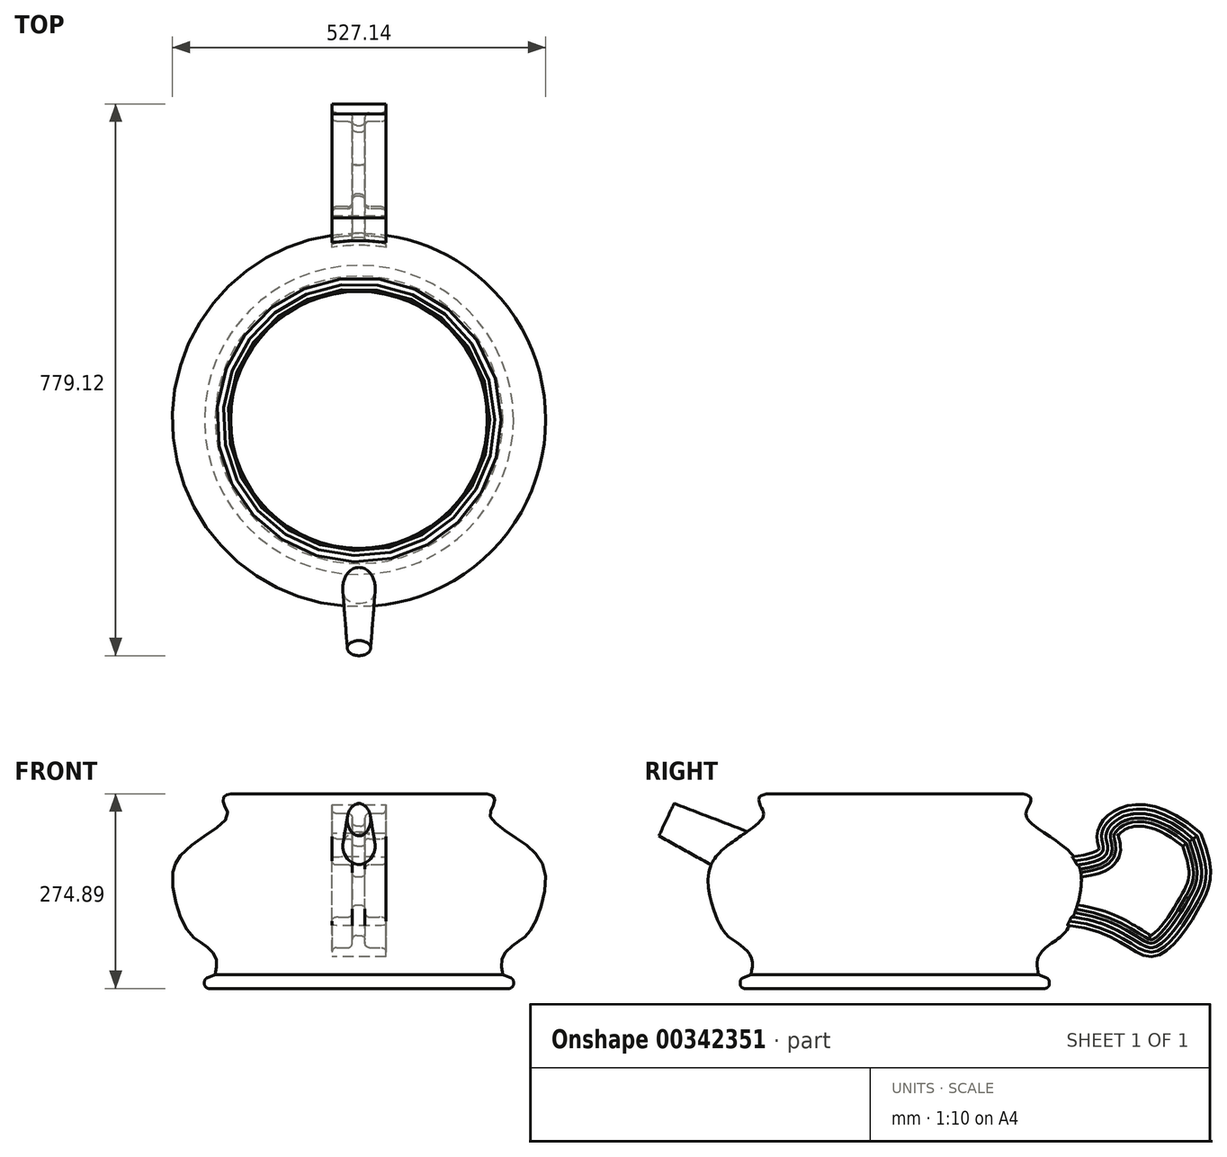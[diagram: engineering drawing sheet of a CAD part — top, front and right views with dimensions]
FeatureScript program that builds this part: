
annotation { "Feature Type Name" : "Feature", "Feature Type Description" : "" }
export const myFeature = defineFeature(function(context is Context, id is Id, definition is map)
    precondition{}
    {
        {
            var Q0;
            Q0=qCreatedBy(makeId("Front.planeOp"),FACE);
            var sketch = newSketch(context, id + "F0", { "sketchPlane" : qUnion([Q0])});
            skLineSegment(sketch, "E0.bottom", {"start": v(-31.75, 4.66) * mm, "end": v(-15.87, 4.66) * mm});
            skLineSegment(sketch, "E0.top", {"start": v(-38.1, -8.04) * mm, "end": v(38.1, -8.04) * mm});
            skLineSegment(sketch, "E0.left", {"start": v(-38.1, -1.7) * mm, "end": v(-38.1, -8.04) * mm});
            skLineSegment(sketch, "E0.right", {"start": v(38.1, -1.7) * mm, "end": v(38.1, -8.04) * mm});
            skPoint(sketch, "E0.middle", {"position": v(0, -1.7) * mm});
            skLineSegment(sketch, "E1", {"start": v(-9.52, 11) * mm, "end": v(-9.52, 16.17) * mm});
            skLineSegment(sketch, "E2", {"start": v(-3.17, 22.52) * mm, "end": v(2.14, 22.52) * mm});
            skLineSegment(sketch, "E3", {"start": v(8.5, 16.17) * mm, "end": v(8.5, 11) * mm});
            skLineSegment(sketch, "E4.trimOffspring", {"start": v(14.84, 4.66) * mm, "end": v(31.75, 4.66) * mm});
            skPoint(sketch, "E5.visualSharp", {"position": v(-9.52, 4.66) * mm});
            skArc(sketch, "E5.filletArc", {"start": v(-15.87, 4.66) * mm, "mid": v(-11.38, 6.52) * mm, "end": v(-9.52, 11) * mm});
            skPoint(sketch, "E6.visualSharp", {"position": v(-38.1, 4.66) * mm});
            skArc(sketch, "E6.filletArc", {"start": v(-31.75, 4.66) * mm, "mid": v(-36.24, 2.8) * mm, "end": v(-38.1, -1.7) * mm});
            skPoint(sketch, "E7.visualSharp", {"position": v(-9.52, 22.52) * mm});
            skArc(sketch, "E7.filletArc", {"start": v(-3.17, 22.52) * mm, "mid": v(-7.66, 20.66) * mm, "end": v(-9.52, 16.17) * mm});
            skPoint(sketch, "E8.visualSharp", {"position": v(8.5, 22.52) * mm});
            skArc(sketch, "E8.filletArc", {"start": v(8.5, 16.17) * mm, "mid": v(6.63, 20.66) * mm, "end": v(2.14, 22.52) * mm});
            skPoint(sketch, "E9.visualSharp", {"position": v(8.5, 4.66) * mm});
            skArc(sketch, "E9.filletArc", {"start": v(8.5, 11) * mm, "mid": v(10.35, 6.52) * mm, "end": v(14.84, 4.66) * mm});
            skPoint(sketch, "E10.visualSharp", {"position": v(38.1, 4.66) * mm});
            skArc(sketch, "E10.filletArc", {"start": v(38.1, -1.7) * mm, "mid": v(36.24, 2.8) * mm, "end": v(31.75, 4.66) * mm});
            skSolve(sketch);
        }
        {
            var Q0;
            Q0=qCreatedBy(makeId("Right.planeOp"),FACE);
            var sketch = newSketch(context, id + "F1", { "sketchPlane" : qUnion([Q0])});
            skFitSpline(sketch, "E11", {"points": [v(0, 0) * mm, v(124.08, -43.75) * mm, v(181.99, 24.07) * mm, v(182.75, 117.02) * mm], "startDerivative": vector(639.17, -56.46) * mm, "endDerivative": vector(-187.27, 486.91) * mm});
            skFitSpline(sketch, "E12", {"points": [v(182.75, 117.02) * mm, v(50.93, 119.3) * mm, v(0, 79.75) * mm], "startDerivative": vector(-384.56, 341.83) * mm, "endDerivative": vector(-537.9, -60.6) * mm});
            skSolve(sketch);
        }
        {
            var Q0;
            Q0=makeQuery(id+"F0.imprint","IMPRINT",FACE,{"disambiguationData":[TD([[makeQuery(id+"F0.imprint","IMPRINT",EDGE,{"derivedFrom":sQuery(id+"F0.wireOp",EDGE,"E0.bottom")}),-1.0]])]});
            var Q1;
            Q1=sQuery(id+"F1.wireOp",EDGE,"E11");
            var Q2;
            Q2=sQuery(id+"F1.wireOp",EDGE,"E12");
            sweep(context, id + "F2", {"profiles" : qUnion([Q0]), "path" : qUnion([Q1, Q2])});
        }
        {
            var Q0;
            Q0=qCreatedBy(makeId("Right.planeOp"),FACE);
            var sketch = newSketch(context, id + "F3", { "sketchPlane" : qUnion([Q0])});
            skFitSpline(sketch, "E13", {"points": [v(-39.6, -77.81) * mm, v(-39.95, -52.85) * mm, v(-18.46, -31.35) * mm, v(0, -14.7) * mm, v(20.03, 66.77) * mm, v(-19.15, 114.27) * mm, v(-57.29, 146.17) * mm, v(-53.13, 160.73) * mm, v(-51.4, 172.52) * mm, v(-61.45, 177.72) * mm], "startDerivative": vector(-55.52, 258.94) * mm, "endDerivative": vector(-190.64, 53.58) * mm});
            skLineSegment(sketch, "E14", {"start": v(-61.45, 177.72) * mm, "end": v(-242.7, 177.72) * mm});
            skLineSegment(sketch, "E15", {"start": v(-242.7, 177.72) * mm, "end": v(-242.7, -77.81) * mm});
            skLineSegment(sketch, "E16", {"start": v(-242.7, -77.81) * mm, "end": v(-242.7, -97.17) * mm});
            skLineSegment(sketch, "E17", {"start": v(-242.7, -97.17) * mm, "end": v(-30.83, -97.17) * mm});
            skLineSegment(sketch, "E18", {"start": v(-24.48, -90.82) * mm, "end": v(-24.48, -87.96) * mm});
            skLineSegment(sketch, "E19", {"start": v(-28.56, -82.02) * mm, "end": v(-39.6, -77.81) * mm});
            skPoint(sketch, "E20.visualSharp", {"position": v(-24.48, -83.58) * mm});
            skArc(sketch, "E20.filletArc", {"start": v(-24.48, -87.96) * mm, "mid": v(-25.6, -84.35) * mm, "end": v(-28.56, -82.02) * mm});
            skPoint(sketch, "E21.visualSharp", {"position": v(-24.48, -97.17) * mm});
            skArc(sketch, "E21.filletArc", {"start": v(-30.83, -97.17) * mm, "mid": v(-26.34, -95.31) * mm, "end": v(-24.48, -90.82) * mm});
            skLineSegment(sketch, "E22", {"start": v(-242.7, 17.38) * mm, "end": v(-242.7, -185.75) * mm, "construction": true});
            skSolve(sketch);
        }
        {
            var Q0;
            Q0=makeQuery(id+"F3.imprint","IMPRINT",FACE,{"disambiguationData":[TD([[makeQuery(id+"F3.imprint","IMPRINT",EDGE,{"derivedFrom":sQuery(id+"F3.wireOp",EDGE,"E13")}),1.0]])]});
            var Q1;
            Q1=sQuery(id+"F3.wireOp",EDGE,"E22");
            revolve(context, id + "F4", {"operationType" : NewBodyOperationType.ADD, "entities" : qUnion([Q0]), "axis" : qUnion([Q1]), "revolveType" : RevolveType.FULL});
        }
        {
            var Q0;
            Q0=qCreatedBy(makeId("Front.planeOp"),FACE);
            cPlane(context, id + "F5", {"entities" : qUnion([Q0]), "cplaneType" : CPlaneType.OFFSET, "offset" : 490.73 * mm, "width" : 152.4 * mm, "height" : 152.4 * mm});
        }
        {
            var Q0;
            Q0=qCreatedBy(id+"F5.planeOp",FACE);
            var sketch = newSketch(context, id + "F6", { "sketchPlane" : qUnion([Q0])});
            skEllipse(sketch, "E23", {"center": v(0, 103.75) * mm, "majorRadius": 60.74 * mm, "minorRadius": 35.53 * mm, "majorAxis": v(0, -1)});
            skSolve(sketch);
        }
        {
            var Q0;
            Q0=qCreatedBy(id+"F5.planeOp",FACE);
            var sketch = newSketch(context, id + "F7", { "sketchPlane" : qUnion([Q0])});
            skLineSegment(sketch, "E24", {"start": v(-73.56, 0) * mm, "end": v(75.93, 0) * mm, "construction": true});
            skSolve(sketch);
        }
        {
            var Q0;
            Q0 = qBodyType(qCreatedBy(id + "F7" ,EDGE), BodyType.WIRE);
            cPlane(context, id + "F8", {"entities" : qUnion([Q0]), "cplaneType" : CPlaneType.LINE_ANGLE, "offset" : 25.4 * mm, "angle" : 25 * degree, "oppositeDirection" : true, "width" : 152.4 * mm, "height" : 152.4 * mm});
        }
        {
            var Q0;
            Q0=qCreatedBy(id+"F8.planeOp",FACE);
            var sketch = newSketch(context, id + "F9", { "sketchPlane" : qUnion([Q0])});
            skEllipse(sketch, "E25", {"center": v(0, -110.82) * mm, "majorRadius": 34.14 * mm, "minorRadius": 25.4 * mm, "majorAxis": v(0, 1)});
            skSolve(sketch);
        }
        {
            var Q0;
            Q0 = qSketchRegion(id + "F9", true);
            extrude(context, id + "F10", {"entities" : qUnion([Q0]), "operationType" : NewBodyOperationType.ADD, "oppositeDirection" : true, "offsetDistance" : 25.4 * mm, "depth" : 127 * mm, "hasDraft" : true, "draftAngle" : 4 * degree, "draftPullDirection" : true});
        }
    });
